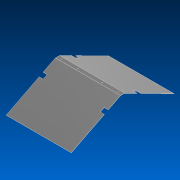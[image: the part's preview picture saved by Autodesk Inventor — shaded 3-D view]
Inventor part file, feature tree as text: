
AUTODESK INVENTOR PART (.ipt)
format: ipt  version: 2022 (Build 260153000, 153)  size: 155,136 bytes
history: native  units: in
note: dims shown in document units (in); Inventor stores cm internally (conversion verified against a paired STEP export)
features: sketch x4, extrude x3, hole x1
ambient origin geometry x8: Origin, YZ Plane, XZ Plane, XY Plane, X Axis, Y Axis, Z Axis, Center Point
bodies: Solid1 (feature_tree)
feature tree (8):
  extrude  "Extrusion1"  Depth=1.0in
  hole  "Hole1"  [1 undecoded]
  extrude  "Extrusion2"  Depth=1.0in
  extrude  "Extrusion3"  Depth=1.0in
  sketch  "Sketch1"  dims[d0=16.0in d1=1.0in]
  sketch  "Sketch2"  dims[d2=0.0625in d3=0.0in d4=1.0in]
  sketch  "Sketch3"  dims[d5=1.0in d6=1.0in]
  sketch  "Sketch4"  dims[d7=1.0in d8=1.0in d9=1.0in d10=3.0in d11=3.0in d12=0.17in d13=0.75in d14=0.375in d15=0.25in d16=0.5635in d17=1.0in d18=0.8108in d19=1.0in d20=4.09in d21=8.1531in d22=7.14in d23=1.0in d24=0.0625in d25=0.0in d26=1.0in d27=0.0in d28=0.0in d29=4.0in]
note: 1 required parameter value undecoded (feature->parameter linkage not recoverable at this tier; creation-order binding heuristic only, values carry confidence <= 0.55)
